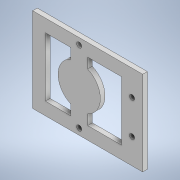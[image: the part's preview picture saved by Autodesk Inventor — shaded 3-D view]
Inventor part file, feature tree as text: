
AUTODESK INVENTOR PART (.ipt)
format: ipt  version: 2022 (Build 260153000, 153)  size: 159,232 bytes
history: native  units: mm
features: extrude x4, sketch x4, other x1
ambient origin geometry x8: Origin, YZ Plane, XZ Plane, XY Plane, X Axis, Y Axis, Z Axis, Center Point
bodies: Body1 (feature_tree)
feature tree (9):
  other  "Sólido1"
  extrude  "Extrusión1"  Depth=100.0mm
  extrude  "Extrusión9"  Depth=70.0mm
  extrude  "Extrusión10"  Depth=20.0mm
  extrude  "Extrusión12"  Depth=5.5mm TaperAngle=0.0deg
  sketch  "Boceto1"  dims[d0=130.0mm d1=100.0mm]
  sketch  "Boceto2"  dims[d2=100.0mm d3=70.0mm]
  sketch  "Boceto8"  dims[d4=5.5mm d5=0.0mm d6=20.0mm]
  sketch  "Boceto9"  dims[d7=10.0mm d30=5.5mm d31=0.0mm d32=20.0mm d33=6.0mm d34=6.0mm d35=5.5mm d36=0.0mm d40=50.0mm d41=5.5mm d42=0.0mm]
